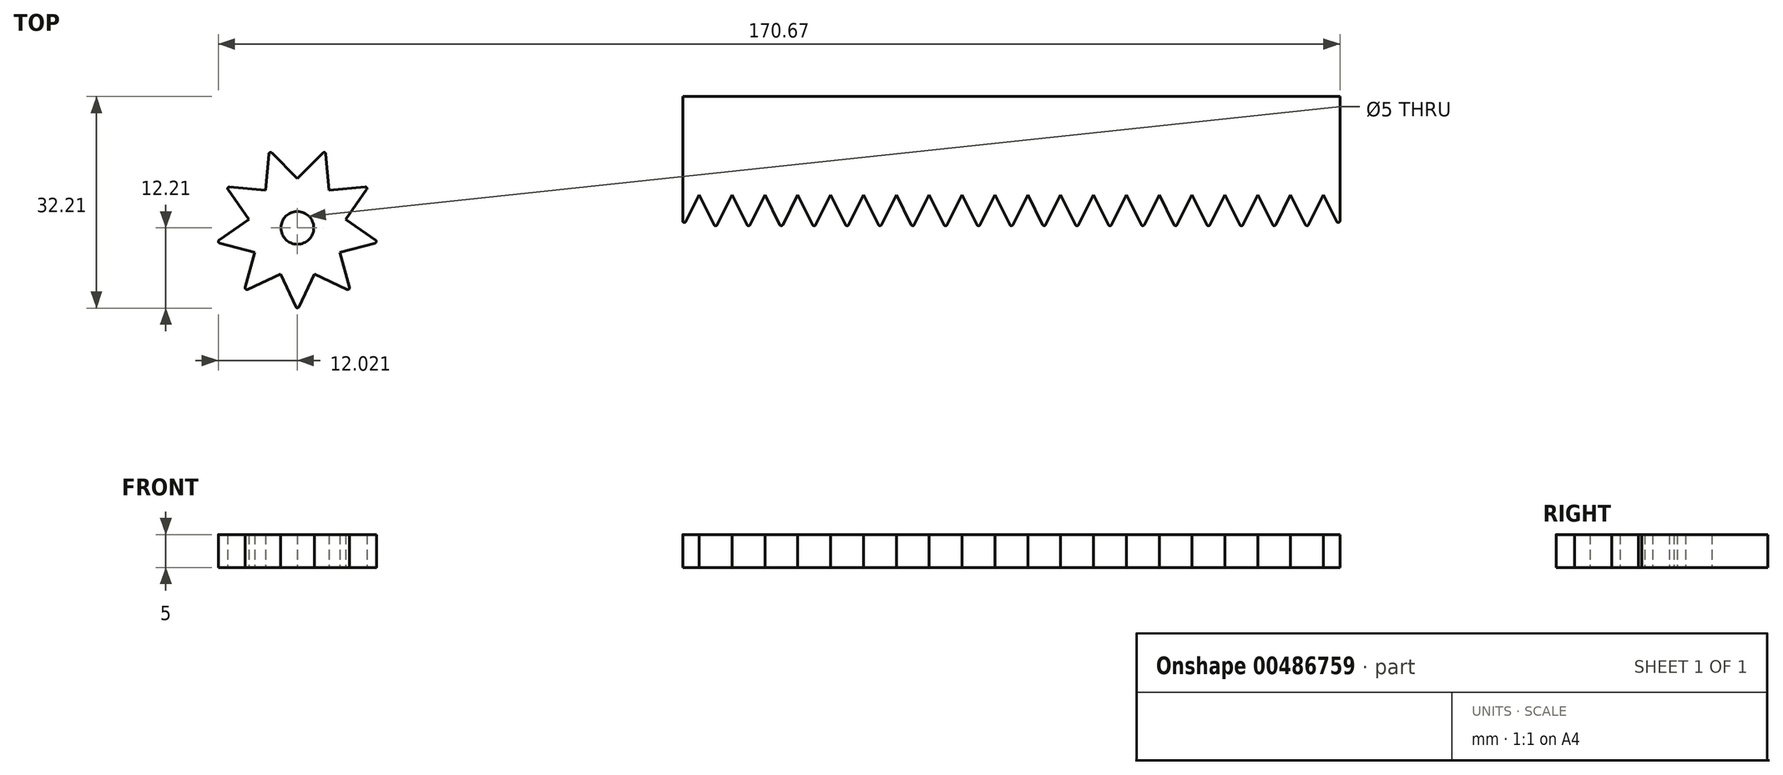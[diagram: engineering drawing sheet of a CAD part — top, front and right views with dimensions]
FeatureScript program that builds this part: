
annotation { "Feature Type Name" : "Feature", "Feature Type Description" : "" }
export const myFeature = defineFeature(function(context is Context, id is Id, definition is map)
    precondition{}
    {
        {
            var Q0;
            Q0=qCreatedBy(makeId("Top.planeOp"),FACE);
            var sketch = newSketch(context, id + "F0", { "sketchPlane" : qUnion([Q0])});
            skLineSegment(sketch, "E0.top", {"start": v(0, 20) * mm, "end": v(100, 20) * mm});
            skLineSegment(sketch, "E0.left", {"start": v(0, 0) * mm, "end": v(0, 20) * mm});
            skLineSegment(sketch, "E0.right", {"start": v(100, 0) * mm, "end": v(100, 20) * mm});
            skLineSegment(sketch, "E1", {"start": v(0, 0) * mm, "end": v(2.5, 5) * mm});
            skLineSegment(sketch, "E2", {"start": v(2.5, 5) * mm, "end": v(5, 0) * mm});
            skLineSegment(sketch, "E3.MirrorCS", {"start": v(7.5, 5) * mm, "end": v(5, 0) * mm});
            skLineSegment(sketch, "E4.MirrorCS", {"start": v(10, 0) * mm, "end": v(7.5, 5) * mm});
            skLineSegment(sketch, "E5.1.0.0", {"start": v(10, 0) * mm, "end": v(12.5, 5) * mm});
            skLineSegment(sketch, "E5.1.0.1", {"start": v(12.5, 5) * mm, "end": v(15, 0) * mm});
            skLineSegment(sketch, "E5.1.0.2", {"start": v(17.5, 5) * mm, "end": v(15, 0) * mm});
            skLineSegment(sketch, "E5.1.0.3", {"start": v(20, 0) * mm, "end": v(17.5, 5) * mm});
            skLineSegment(sketch, "E5.2.0.0", {"start": v(20, 0) * mm, "end": v(22.5, 5) * mm});
            skLineSegment(sketch, "E5.2.0.1", {"start": v(22.5, 5) * mm, "end": v(25, 0) * mm});
            skLineSegment(sketch, "E5.2.0.2", {"start": v(27.5, 5) * mm, "end": v(25, 0) * mm});
            skLineSegment(sketch, "E5.2.0.3", {"start": v(30, 0) * mm, "end": v(27.5, 5) * mm});
            skLineSegment(sketch, "E6.1.0.0", {"start": v(60, 0) * mm, "end": v(57.5, 5) * mm});
            skLineSegment(sketch, "E6.1.0.1", {"start": v(57.5, 5) * mm, "end": v(55, 0) * mm});
            skLineSegment(sketch, "E6.1.0.2", {"start": v(52.5, 5) * mm, "end": v(55, 0) * mm});
            skLineSegment(sketch, "E6.1.0.3", {"start": v(50, 0) * mm, "end": v(52.5, 5) * mm});
            skLineSegment(sketch, "E6.1.0.4", {"start": v(50, 0) * mm, "end": v(47.5, 5) * mm});
            skLineSegment(sketch, "E6.1.0.5", {"start": v(47.5, 5) * mm, "end": v(45, 0) * mm});
            skLineSegment(sketch, "E6.1.0.6", {"start": v(42.5, 5) * mm, "end": v(45, 0) * mm});
            skLineSegment(sketch, "E6.1.0.7", {"start": v(40, 0) * mm, "end": v(42.5, 5) * mm});
            skLineSegment(sketch, "E6.1.0.8", {"start": v(40, 0) * mm, "end": v(37.5, 5) * mm});
            skLineSegment(sketch, "E6.1.0.9", {"start": v(37.5, 5) * mm, "end": v(35, 0) * mm});
            skLineSegment(sketch, "E6.1.0.10", {"start": v(32.5, 5) * mm, "end": v(35, 0) * mm});
            skLineSegment(sketch, "E6.1.0.11", {"start": v(30, 0) * mm, "end": v(32.5, 5) * mm});
            skLineSegment(sketch, "E6.2.0.0", {"start": v(90, 0) * mm, "end": v(87.5, 5) * mm});
            skLineSegment(sketch, "E6.2.0.1", {"start": v(87.5, 5) * mm, "end": v(85, 0) * mm});
            skLineSegment(sketch, "E6.2.0.2", {"start": v(82.5, 5) * mm, "end": v(85, 0) * mm});
            skLineSegment(sketch, "E6.2.0.3", {"start": v(80, 0) * mm, "end": v(82.5, 5) * mm});
            skLineSegment(sketch, "E6.2.0.4", {"start": v(80, 0) * mm, "end": v(77.5, 5) * mm});
            skLineSegment(sketch, "E6.2.0.5", {"start": v(77.5, 5) * mm, "end": v(75, 0) * mm});
            skLineSegment(sketch, "E6.2.0.6", {"start": v(72.5, 5) * mm, "end": v(75, 0) * mm});
            skLineSegment(sketch, "E6.2.0.7", {"start": v(70, 0) * mm, "end": v(72.5, 5) * mm});
            skLineSegment(sketch, "E6.2.0.8", {"start": v(70, 0) * mm, "end": v(67.5, 5) * mm});
            skLineSegment(sketch, "E6.2.0.9", {"start": v(67.5, 5) * mm, "end": v(65, 0) * mm});
            skLineSegment(sketch, "E6.2.0.10", {"start": v(62.5, 5) * mm, "end": v(65, 0) * mm});
            skLineSegment(sketch, "E6.2.0.11", {"start": v(60, 0) * mm, "end": v(62.5, 5) * mm});
            skLineSegment(sketch, "E7.1.0.0", {"start": v(95, 0) * mm, "end": v(92.5, 5) * mm});
            skLineSegment(sketch, "E7.1.0.1", {"start": v(92.5, 5) * mm, "end": v(90, 0) * mm});
            skLineSegment(sketch, "E7.2.0.0", {"start": v(100, 0) * mm, "end": v(97.5, 5) * mm});
            skLineSegment(sketch, "E7.2.0.1", {"start": v(97.5, 5) * mm, "end": v(95, 0) * mm});
            skSolve(sketch);
        }
        {
            var Q0;
            Q0 = qSketchRegion(id + "F0", true);
            extrude(context, id + "F1", {"entities" : qUnion([Q0]), "depth" : 5 * mm});
        }
        {
            var Q0;
            Q0=makeQuery(id+"F1.opExtrude","SWEPT_EDGE",EDGE,{"disambiguationData":[OSD([sQuery(id+"F0.wireOp",EDGE,"E3.MirrorCS"),sQuery(id+"F0.wireOp",EDGE,"E2")])]});
            var Q1;
            Q1=makeQuery(id+"F1.opExtrude","SWEPT_EDGE",EDGE,{"disambiguationData":[OSD([sQuery(id+"F0.wireOp",EDGE,"E4.MirrorCS"),sQuery(id+"F0.wireOp",EDGE,"E5.1.0.0")])]});
            var Q2;
            Q2=makeQuery(id+"F1.opExtrude","SWEPT_EDGE",EDGE,{"disambiguationData":[OSD([sQuery(id+"F0.wireOp",EDGE,"E5.1.0.1"),sQuery(id+"F0.wireOp",EDGE,"E5.1.0.2")])]});
            var Q3;
            Q3=makeQuery(id+"F1.opExtrude","SWEPT_EDGE",EDGE,{"disambiguationData":[OSD([sQuery(id+"F0.wireOp",EDGE,"E0.left"),sQuery(id+"F0.wireOp",EDGE,"E1")])]});
            var Q4;
            Q4=makeQuery(id+"F1.opExtrude","SWEPT_EDGE",EDGE,{"disambiguationData":[OSD([sQuery(id+"F0.wireOp",EDGE,"E5.1.0.3"),sQuery(id+"F0.wireOp",EDGE,"E5.2.0.0")])]});
            var Q5;
            Q5=makeQuery(id+"F1.opExtrude","SWEPT_EDGE",EDGE,{"disambiguationData":[OSD([sQuery(id+"F0.wireOp",EDGE,"E5.2.0.1"),sQuery(id+"F0.wireOp",EDGE,"E5.2.0.2")])]});
            var Q6;
            Q6=makeQuery(id+"F1.opExtrude","SWEPT_EDGE",EDGE,{"disambiguationData":[OSD([sQuery(id+"F0.wireOp",EDGE,"E5.2.0.3"),sQuery(id+"F0.wireOp",EDGE,"E6.1.0.11")])]});
            var Q7;
            Q7=makeQuery(id+"F1.opExtrude","SWEPT_EDGE",EDGE,{"disambiguationData":[OSD([sQuery(id+"F0.wireOp",EDGE,"E6.1.0.9"),sQuery(id+"F0.wireOp",EDGE,"E6.1.0.10")])]});
            var Q8;
            Q8=makeQuery(id+"F1.opExtrude","SWEPT_EDGE",EDGE,{"disambiguationData":[OSD([sQuery(id+"F0.wireOp",EDGE,"E6.1.0.7"),sQuery(id+"F0.wireOp",EDGE,"E6.1.0.8")])]});
            var Q9;
            Q9=makeQuery(id+"F1.opExtrude","SWEPT_EDGE",EDGE,{"disambiguationData":[OSD([sQuery(id+"F0.wireOp",EDGE,"E6.1.0.5"),sQuery(id+"F0.wireOp",EDGE,"E6.1.0.6")])]});
            var Q10;
            Q10=makeQuery(id+"F1.opExtrude","SWEPT_EDGE",EDGE,{"disambiguationData":[OSD([sQuery(id+"F0.wireOp",EDGE,"E6.1.0.3"),sQuery(id+"F0.wireOp",EDGE,"E6.1.0.4")])]});
            var Q11;
            Q11=makeQuery(id+"F1.opExtrude","SWEPT_EDGE",EDGE,{"disambiguationData":[OSD([sQuery(id+"F0.wireOp",EDGE,"E6.1.0.1"),sQuery(id+"F0.wireOp",EDGE,"E6.1.0.2")])]});
            var Q12;
            Q12=makeQuery(id+"F1.opExtrude","SWEPT_EDGE",EDGE,{"disambiguationData":[OSD([sQuery(id+"F0.wireOp",EDGE,"E6.1.0.0"),sQuery(id+"F0.wireOp",EDGE,"E6.2.0.11")])]});
            var Q13;
            Q13=makeQuery(id+"F1.opExtrude","SWEPT_EDGE",EDGE,{"disambiguationData":[OSD([sQuery(id+"F0.wireOp",EDGE,"E6.2.0.9"),sQuery(id+"F0.wireOp",EDGE,"E6.2.0.10")])]});
            var Q14;
            Q14=makeQuery(id+"F1.opExtrude","SWEPT_EDGE",EDGE,{"disambiguationData":[OSD([sQuery(id+"F0.wireOp",EDGE,"E6.2.0.7"),sQuery(id+"F0.wireOp",EDGE,"E6.2.0.8")])]});
            var Q15;
            Q15=makeQuery(id+"F1.opExtrude","SWEPT_EDGE",EDGE,{"disambiguationData":[OSD([sQuery(id+"F0.wireOp",EDGE,"E6.2.0.3"),sQuery(id+"F0.wireOp",EDGE,"E6.2.0.4")])]});
            var Q16;
            Q16=makeQuery(id+"F1.opExtrude","SWEPT_EDGE",EDGE,{"disambiguationData":[OSD([sQuery(id+"F0.wireOp",EDGE,"E6.2.0.1"),sQuery(id+"F0.wireOp",EDGE,"E6.2.0.2")])]});
            var Q17;
            Q17=makeQuery(id+"F1.opExtrude","SWEPT_EDGE",EDGE,{"disambiguationData":[OSD([sQuery(id+"F0.wireOp",EDGE,"E6.2.0.0"),sQuery(id+"F0.wireOp",EDGE,"E7.1.0.1")])]});
            var Q18;
            Q18=makeQuery(id+"F1.opExtrude","SWEPT_EDGE",EDGE,{"disambiguationData":[OSD([sQuery(id+"F0.wireOp",EDGE,"E7.1.0.0"),sQuery(id+"F0.wireOp",EDGE,"E7.2.0.1")])]});
            var Q19;
            Q19=makeQuery(id+"F1.opExtrude","SWEPT_EDGE",EDGE,{"disambiguationData":[OSD([sQuery(id+"F0.wireOp",EDGE,"E0.right"),sQuery(id+"F0.wireOp",EDGE,"E7.2.0.0")])]});
            var Q20;
            Q20=makeQuery(id+"F1.opExtrude","SWEPT_EDGE",EDGE,{"disambiguationData":[OSD([sQuery(id+"F0.wireOp",EDGE,"E6.2.0.5"),sQuery(id+"F0.wireOp",EDGE,"E6.2.0.6")])]});
            fillet(context, id + "F2", {"entities" : qUnion([Q0, Q1, Q2, Q3, Q4, Q5, Q6, Q7, Q8, Q9, Q10, Q11, Q12, Q13, Q14, Q15, Q16, Q17, Q18, Q19, Q20]), "radius" : 0.25 * mm, "tangentPropagation" : true, "allowEdgeOverflow" : false});
        }
        {
            var Q0;
            Q0=qCreatedBy(makeId("Top.planeOp"),FACE);
            var sketch = newSketch(context, id + "F3", { "sketchPlane" : qUnion([Q0])});
            skLineSegment(sketch, "E8", {"start": v(-54.36, 11.8) * mm, "end": v(-58.65, 7.5) * mm});
            skLineSegment(sketch, "E9", {"start": v(-58.65, 7.5) * mm, "end": v(-62.94, 11.8) * mm});
            skLineSegment(sketch, "E10.1.0", {"start": v(-63.47, 5.75) * mm, "end": v(-69.52, 6.27) * mm});
            skLineSegment(sketch, "E10.1.1", {"start": v(-62.94, 11.8) * mm, "end": v(-63.47, 5.75) * mm});
            skLineSegment(sketch, "E10.2.0", {"start": v(-66.04, 1.3) * mm, "end": v(-71, -2.18) * mm});
            skLineSegment(sketch, "E10.2.1", {"start": v(-69.52, 6.27) * mm, "end": v(-66.04, 1.3) * mm});
            skLineSegment(sketch, "E10.3.0", {"start": v(-65.14, -3.75) * mm, "end": v(-66.72, -9.61) * mm});
            skLineSegment(sketch, "E10.3.1", {"start": v(-71, -2.18) * mm, "end": v(-65.14, -3.75) * mm});
            skLineSegment(sketch, "E10.4.0", {"start": v(-61.21, -7.05) * mm, "end": v(-58.65, -12.55) * mm});
            skLineSegment(sketch, "E10.4.1", {"start": v(-66.72, -9.61) * mm, "end": v(-61.21, -7.05) * mm});
            skLineSegment(sketch, "E10.5.0", {"start": v(-56.08, -7.05) * mm, "end": v(-50.58, -9.61) * mm});
            skLineSegment(sketch, "E10.5.1", {"start": v(-58.65, -12.55) * mm, "end": v(-56.08, -7.05) * mm});
            skLineSegment(sketch, "E10.6.0", {"start": v(-52.15, -3.75) * mm, "end": v(-46.3, -2.18) * mm});
            skLineSegment(sketch, "E10.6.1", {"start": v(-50.58, -9.61) * mm, "end": v(-52.15, -3.75) * mm});
            skLineSegment(sketch, "E10.7.0", {"start": v(-51.26, 1.3) * mm, "end": v(-47.78, 6.27) * mm});
            skLineSegment(sketch, "E10.7.1", {"start": v(-46.3, -2.18) * mm, "end": v(-51.26, 1.3) * mm});
            skLineSegment(sketch, "E10.8.0", {"start": v(-53.83, 5.75) * mm, "end": v(-54.36, 11.8) * mm});
            skLineSegment(sketch, "E10.8.1", {"start": v(-47.78, 6.27) * mm, "end": v(-53.83, 5.75) * mm});
            skPoint(sketch, "E10.center", {"position": v(-58.65, 0) * mm});
            skCircle(sketch, "E11", {"center": v(-58.65, 0) * mm, "radius": 2.5 * mm});
            skPoint(sketch, "E12.orphan", {"position": v(-62.85, 12.79) * mm});
            skPoint(sketch, "E13.orphan", {"position": v(-63.65, 12.5) * mm});
            skPoint(sketch, "E14.orphan", {"position": v(-54.44, 12.79) * mm});
            skPoint(sketch, "E15.orphan", {"position": v(-53.65, 12.5) * mm});
            skPoint(sketch, "E16.orphan", {"position": v(-47.2, 7.1) * mm});
            skPoint(sketch, "E17.orphan", {"position": v(-46.78, 6.36) * mm});
            skPoint(sketch, "E18.orphan", {"position": v(-45.32, -1.92) * mm});
            skPoint(sketch, "E19.orphan", {"position": v(-45.47, -2.75) * mm});
            skPoint(sketch, "E20.orphan", {"position": v(-70.1, 7.1) * mm});
            skPoint(sketch, "E21.orphan", {"position": v(-70.51, 6.36) * mm});
            skPoint(sketch, "E22.orphan", {"position": v(-71.97, -1.92) * mm});
            skPoint(sketch, "E23.orphan", {"position": v(-71.83, -2.75) * mm});
            skPoint(sketch, "E24.orphan", {"position": v(-67.62, -10.04) * mm});
            skPoint(sketch, "E25.orphan", {"position": v(-66.97, -10.58) * mm});
            skPoint(sketch, "E26.orphan", {"position": v(-59.07, -13.46) * mm});
            skPoint(sketch, "E27.orphan", {"position": v(-58.23, -13.46) * mm});
            skPoint(sketch, "E28.orphan", {"position": v(-50.32, -10.58) * mm});
            skPoint(sketch, "E29.orphan", {"position": v(-49.68, -10.04) * mm});
            skSolve(sketch);
        }
        {
            var Q0;
            Q0=makeQuery(id+"F3.imprint","IMPRINT",FACE,{"disambiguationData":[TD([[makeQuery(id+"F3.imprint","IMPRINT",EDGE,{"derivedFrom":sQuery(id+"F3.wireOp",EDGE,"E8")}),1.0]])]});
            extrude(context, id + "F4", {"entities" : qUnion([Q0]), "depth" : 5 * mm});
        }
        {
            var Q0;
            Q0=makeQuery(id+"F4.opExtrude","SWEPT_EDGE",EDGE,{"disambiguationData":[OSD([sQuery(id+"F3.wireOp",EDGE,"E9"),sQuery(id+"F3.wireOp",EDGE,"E10.1.1")])]});
            var Q1;
            Q1=makeQuery(id+"F4.opExtrude","SWEPT_EDGE",EDGE,{"disambiguationData":[OSD([sQuery(id+"F3.wireOp",EDGE,"E8"),sQuery(id+"F3.wireOp",EDGE,"E10.8.0")])]});
            var Q2;
            Q2=makeQuery(id+"F4.opExtrude","SWEPT_EDGE",EDGE,{"disambiguationData":[OSD([sQuery(id+"F3.wireOp",EDGE,"E10.7.0"),sQuery(id+"F3.wireOp",EDGE,"E10.8.1")])]});
            var Q3;
            Q3=makeQuery(id+"F4.opExtrude","SWEPT_EDGE",EDGE,{"disambiguationData":[OSD([sQuery(id+"F3.wireOp",EDGE,"E10.6.0"),sQuery(id+"F3.wireOp",EDGE,"E10.7.1")])]});
            var Q4;
            Q4=makeQuery(id+"F4.opExtrude","SWEPT_EDGE",EDGE,{"disambiguationData":[OSD([sQuery(id+"F3.wireOp",EDGE,"E10.5.0"),sQuery(id+"F3.wireOp",EDGE,"E10.6.1")])]});
            var Q5;
            Q5=makeQuery(id+"F4.opExtrude","SWEPT_EDGE",EDGE,{"disambiguationData":[OSD([sQuery(id+"F3.wireOp",EDGE,"E10.4.0"),sQuery(id+"F3.wireOp",EDGE,"E10.5.1")])]});
            var Q6;
            Q6=makeQuery(id+"F4.opExtrude","SWEPT_EDGE",EDGE,{"disambiguationData":[OSD([sQuery(id+"F3.wireOp",EDGE,"E10.3.0"),sQuery(id+"F3.wireOp",EDGE,"E10.4.1")])]});
            var Q7;
            Q7=makeQuery(id+"F4.opExtrude","SWEPT_EDGE",EDGE,{"disambiguationData":[OSD([sQuery(id+"F3.wireOp",EDGE,"E10.2.0"),sQuery(id+"F3.wireOp",EDGE,"E10.3.1")])]});
            var Q8;
            Q8=makeQuery(id+"F4.opExtrude","SWEPT_EDGE",EDGE,{"disambiguationData":[OSD([sQuery(id+"F3.wireOp",EDGE,"E10.1.0"),sQuery(id+"F3.wireOp",EDGE,"E10.2.1")])]});
            fillet(context, id + "F5", {"entities" : qUnion([Q0, Q1, Q2, Q3, Q4, Q5, Q6, Q7, Q8]), "radius" : 0.25 * mm, "tangentPropagation" : true, "allowEdgeOverflow" : false});
        }
    });
